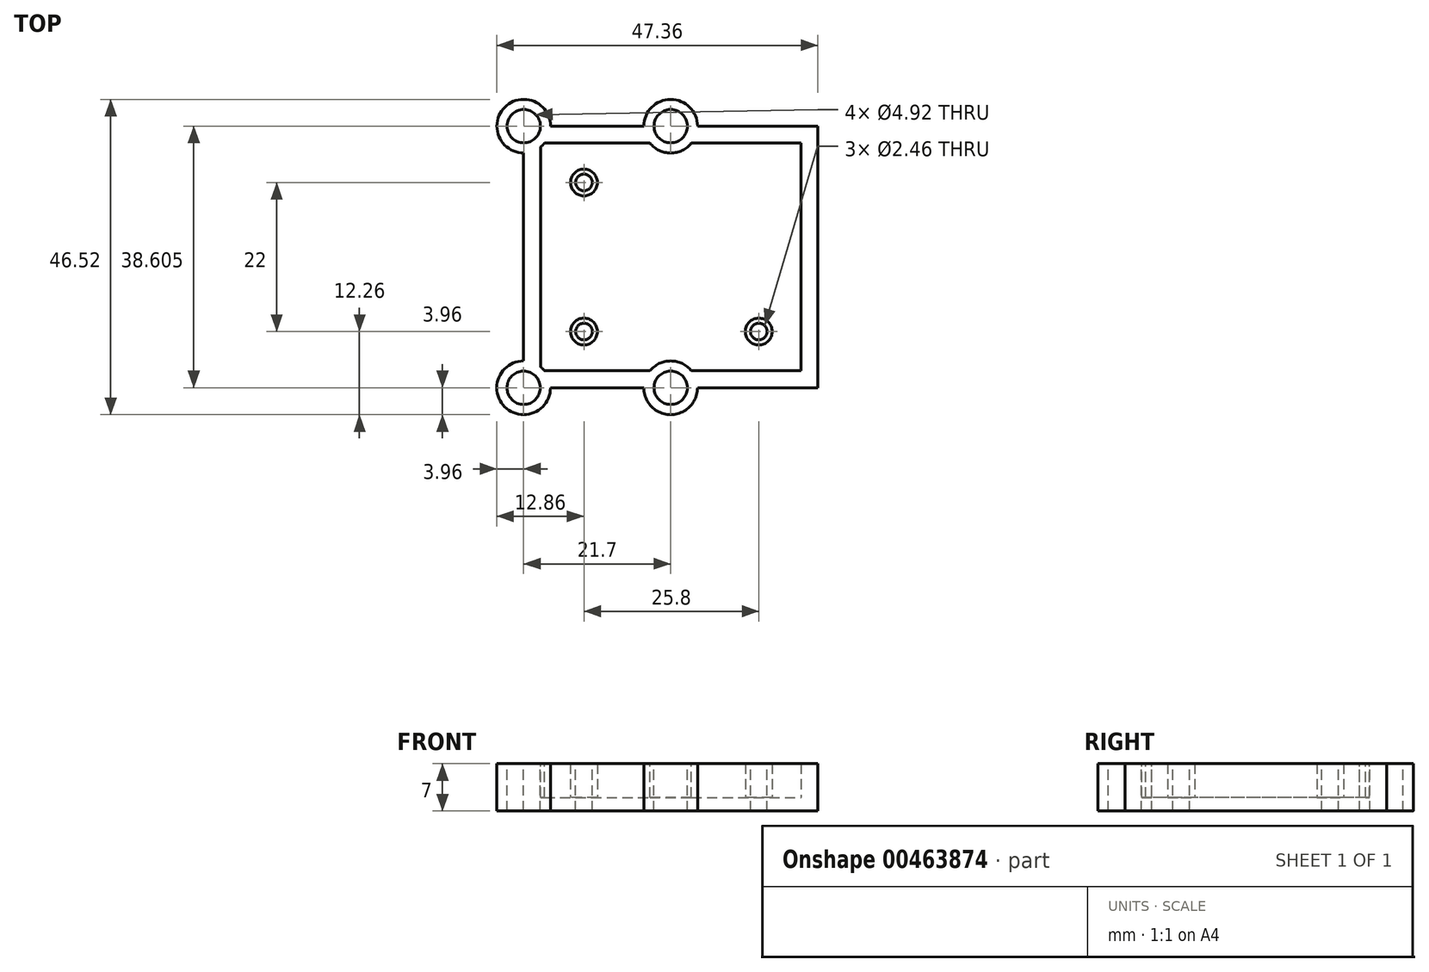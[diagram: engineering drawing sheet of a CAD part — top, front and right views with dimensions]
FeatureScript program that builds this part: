
annotation { "Feature Type Name" : "Feature", "Feature Type Description" : "" }
export const myFeature = defineFeature(function(context is Context, id is Id, definition is map)
    precondition{}
    {
        {
            assignVariable(context, id + "F0", {"name" : "Drill_Diam_Box", "anyValue" : 4.92});
        }
        {
            assignVariable(context, id + "F1", {"name" : "Drill_Diam", "anyValue" : 2.46});
        }
        {
            assignVariable(context, id + "F2", {"name" : "Longueur_Vis_Carte", "anyValue" : 5});
        }
        {
            assignVariable(context, id + "F3", {"name" : "Hauteur_Boitier_Bot", "anyValue" : 2 + getVariable(context, 'Longueur_Vis_Carte')});
        }
        {
            assignVariable(context, id + "F4", {"name" : "Socle_Boitier", "anyValue" : 2});
        }
        {
            var Q0;
            Q0=qCreatedBy(makeId("Top.planeOp"),FACE);
            var sketch = newSketch(context, id + "F5", { "sketchPlane" : qUnion([Q0])});
            skPoint(sketch, "E0.middle", {"position": v(0, 0) * mm});
            skPoint(sketch, "E1", {"position": v(-12.8, 11) * mm});
            skPoint(sketch, "E2", {"position": v(13, -11) * mm});
            skCircle(sketch, "E3", {"center": v(-12.8, 11) * mm, "radius": 1.23 * mm});
            skCircle(sketch, "E4", {"center": v(13, -11) * mm, "radius": 1.23 * mm});
            skSolve(sketch);
        }
        {
            var Q0;
            Q0=qCreatedBy(makeId("Top.planeOp"),FACE);
            var sketch = newSketch(context, id + "F6", { "sketchPlane" : qUnion([Q0])});
            skLineSegment(sketch, "E5.bottom", {"start": v(-19.2, 16.8) * mm, "end": v(19.2, 16.8) * mm});
            skLineSegment(sketch, "E5.top", {"start": v(-19.2, -16.8) * mm, "end": v(19.2, -16.8) * mm});
            skLineSegment(sketch, "E5.left", {"start": v(-19.2, 16.8) * mm, "end": v(-19.2, -16.8) * mm});
            skLineSegment(sketch, "E5.right", {"start": v(19.2, 16.8) * mm, "end": v(19.2, -16.8) * mm});
            skPoint(sketch, "E5.middle", {"position": v(0, 0) * mm});
            skSolve(sketch);
        }
        {
            var Q0;
            Q0=qCreatedBy(makeId("Top.planeOp"),FACE);
            var sketch = newSketch(context, id + "F7", { "sketchPlane" : qUnion([Q0])});
            skLineSegment(sketch, "E6.bottom", {"start": v(-21.7, 19.3) * mm, "end": v(21.7, 19.3) * mm});
            skLineSegment(sketch, "E6.top", {"start": v(-21.7, -19.3) * mm, "end": v(21.7, -19.3) * mm});
            skLineSegment(sketch, "E6.left", {"start": v(-21.7, 19.3) * mm, "end": v(-21.7, -19.3) * mm});
            skLineSegment(sketch, "E6.right", {"start": v(21.7, 19.3) * mm, "end": v(21.7, -19.3) * mm});
            skPoint(sketch, "E6.middle", {"position": v(0, 0) * mm});
            skSolve(sketch);
        }
        {
            var Q0;
            Q0 = qSketchRegion(id + "F7", true);
            extrude(context, id + "F8", {"entities" : qUnion([Q0]), "depth" : (getVariable(context, 'Hauteur_Boitier_Bot')) * mm});
        }
        {
            var Q0;
            Q0 = qSketchRegion(id + "F6", true);
            extrude(context, id + "F9", {"entities" : qUnion([Q0]), "operationType" : NewBodyOperationType.REMOVE, "depth" : (getVariable(context, 'Hauteur_Boitier_Bot')) * mm});
        }
        {
            var Q0;
            Q0 = qSketchRegion(id + "F6", true);
            extrude(context, id + "F10", {"entities" : qUnion([Q0]), "operationType" : NewBodyOperationType.ADD, "depth" : (getVariable(context, 'Socle_Boitier')) * mm});
        }
        {
            var Q0;
            Q0=makeQuery(id+"F10.opExtrude","CAP_FACE",FACE,{"disambiguationData":[OSD([sQuery(id+"F6.wireOp",EDGE,"E5.bottom"),sQuery(id+"F6.wireOp",EDGE,"E5.top"),sQuery(id+"F6.wireOp",EDGE,"E5.left"),sQuery(id+"F6.wireOp",EDGE,"E5.right")])],"isStart":false});
            var sketch = newSketch(context, id + "F11", { "sketchPlane" : qUnion([Q0])});
            skPoint(sketch, "E7", {"position": v(-12.8, 11) * mm});
            skCircle(sketch, "E8", {"center": v(-12.8, 11) * mm, "radius": 1.98 * mm});
            skPoint(sketch, "E9", {"position": v(13, -11) * mm});
            skCircle(sketch, "E10", {"center": v(13, -11) * mm, "radius": 1.98 * mm});
            skPoint(sketch, "E11", {"position": v(-12.8, -11) * mm});
            skCircle(sketch, "E12", {"center": v(-12.8, -11) * mm, "radius": 1.98 * mm});
            skSolve(sketch);
        }
        {
            var Q0;
            Q0 = qSketchRegion(id + "F11", true);
            extrude(context, id + "F12", {"entities" : qUnion([Q0]), "operationType" : NewBodyOperationType.ADD, "depth" : (getVariable(context, 'Longueur_Vis_Carte')) * mm, "offsetDistance" : 25 * mm});
        }
        {
            var Q0;
            Q0=makeQuery(id+"F8.opExtrude","SWEPT_BODY",BODY,{"disambiguationData":[OSD([sQuery(id+"F7.wireOp",EDGE,"E6.bottom"),sQuery(id+"F7.wireOp",EDGE,"E6.top"),sQuery(id+"F7.wireOp",EDGE,"E6.left"),sQuery(id+"F7.wireOp",EDGE,"E6.right")])]});
            transform(context, id + "F13", {"entities" : qUnion([Q0]), "transformType" : TransformType.TRANSLATION_3D, "dx" : 0 * mm, "dy" : 0 * mm, "dz" : (-getVariable(context, 'Hauteur_Boitier_Bot')) * mm, "makeCopy" : false});
        }
        {
            var Q0;
            Q0=makeQuery(id+"F8.opExtrude","CAP_FACE",FACE,{"disambiguationData":[OSD([sQuery(id+"F7.wireOp",EDGE,"E6.bottom"),sQuery(id+"F7.wireOp",EDGE,"E6.top"),sQuery(id+"F7.wireOp",EDGE,"E6.left"),sQuery(id+"F7.wireOp",EDGE,"E6.right")])],"isStart":false});
            var sketch = newSketch(context, id + "F14", { "sketchPlane" : qUnion([Q0])});
            skLineSegment(sketch, "E13.bottom", {"start": v(-20.45, 18.05) * mm, "end": v(20.45, 18.05) * mm});
            skLineSegment(sketch, "E13.top", {"start": v(-20.45, -18.05) * mm, "end": v(20.45, -18.05) * mm});
            skLineSegment(sketch, "E13.left", {"start": v(-20.45, 18.05) * mm, "end": v(-20.45, -18.05) * mm});
            skLineSegment(sketch, "E13.right", {"start": v(20.45, 18.05) * mm, "end": v(20.45, -18.05) * mm});
            skPoint(sketch, "E13.middle", {"position": v(0, 0) * mm});
            skPoint(sketch, "E14", {"position": v(-20.45, 18.05) * mm});
            skPoint(sketch, "E15", {"position": v(20.45, 18.05) * mm});
            skPoint(sketch, "E16", {"position": v(20.45, -18.05) * mm});
            skPoint(sketch, "E17", {"position": v(-20.45, -18.05) * mm});
            skSolve(sketch);
        }
        {
            var Q0;
            Q0=makeQuery(id+"F14.imprint","IMPRINT",FACE,{"disambiguationData":[TD([[makeQuery(id+"F14.imprint","IMPRINT",EDGE,{"derivedFrom":sQuery(id+"F14.wireOp",EDGE,"E13.bottom")}),1.0]])]});
            var sketch = newSketch(context, id + "F15", { "sketchPlane" : qUnion([Q0])});
            skPoint(sketch, "E18", {"position": v(-21.69, 19.3) * mm});
            skPoint(sketch, "E19", {"position": v(0, 19.3) * mm});
            skPoint(sketch, "E20", {"position": v(0, -19.3) * mm});
            skPoint(sketch, "E21", {"position": v(-21.7, -19.3) * mm});
            skCircle(sketch, "E22", {"center": v(-21.7, -19.3) * mm, "radius": 3.96 * mm});
            skCircle(sketch, "E23", {"center": v(0, -19.3) * mm, "radius": 3.96 * mm});
            skCircle(sketch, "E24", {"center": v(0, 19.3) * mm, "radius": 3.96 * mm});
            skCircle(sketch, "E25", {"center": v(-21.69, 19.3) * mm, "radius": 3.96 * mm});
            skSolve(sketch);
        }
        {
            var Q0;
            Q0 = qSketchRegion(id + "F15", true);
            extrude(context, id + "F16", {"entities" : qUnion([Q0]), "operationType" : NewBodyOperationType.ADD, "oppositeDirection" : true, "depth" : (getVariable(context, 'Hauteur_Boitier_Bot')) * mm});
        }
        {
            var Q0;
            Q0=sQuery(id+"F15.wireOp",VERTEX,"E18");
            var Q1;
            Q1=sQuery(id+"F15.wireOp",VERTEX,"E19");
            var Q2;
            Q2=sQuery(id+"F15.wireOp",VERTEX,"E20");
            var Q3;
            Q3=sQuery(id+"F15.wireOp",VERTEX,"E21");
            var Q4;
            Q4=makeQuery(id+"F8.opExtrude","SWEPT_BODY",BODY,{"disambiguationData":[OSD([sQuery(id+"F7.wireOp",EDGE,"E6.bottom"),sQuery(id+"F7.wireOp",EDGE,"E6.top"),sQuery(id+"F7.wireOp",EDGE,"E6.left"),sQuery(id+"F7.wireOp",EDGE,"E6.right")])]});
            hole(context, id + "F17", {"style" : HoleStyle.SIMPLE, "endStyle" : HoleEndStyle.THROUGH, "holeDiameter" : (getVariable(context, 'Drill_Diam_Box')) * mm, "isTappedThrough" : true, "tappedDepth" : 12 * mm, "tapClearance" : 3, "startFromSketch" : true, "locations" : qUnion([Q0, Q1, Q2, Q3]), "scope" : qUnion([Q4])});
        }
        {
            var Q0;
            Q0=sQuery(id+"F5.wireOp",VERTEX,"E1");
            var Q1;
            Q1=sQuery(id+"F5.wireOp",VERTEX,"E2");
            var Q2;
            Q2=sQuery(id+"F11.wireOp",VERTEX,"E11");
            var Q3;
            Q3=makeQuery(id+"F8.opExtrude","SWEPT_BODY",BODY,{"disambiguationData":[OSD([sQuery(id+"F7.wireOp",EDGE,"E6.bottom"),sQuery(id+"F7.wireOp",EDGE,"E6.top"),sQuery(id+"F7.wireOp",EDGE,"E6.left"),sQuery(id+"F7.wireOp",EDGE,"E6.right")])]});
            hole(context, id + "F18", {"style" : HoleStyle.SIMPLE, "endStyle" : HoleEndStyle.THROUGH, "holeDiameter" : (getVariable(context, 'Drill_Diam')) * mm, "isTappedThrough" : true, "tappedDepth" : 12 * mm, "tapClearance" : 3, "startFromSketch" : true, "locations" : qUnion([Q0, Q1, Q2]), "scope" : qUnion([Q3])});
        }
    });
